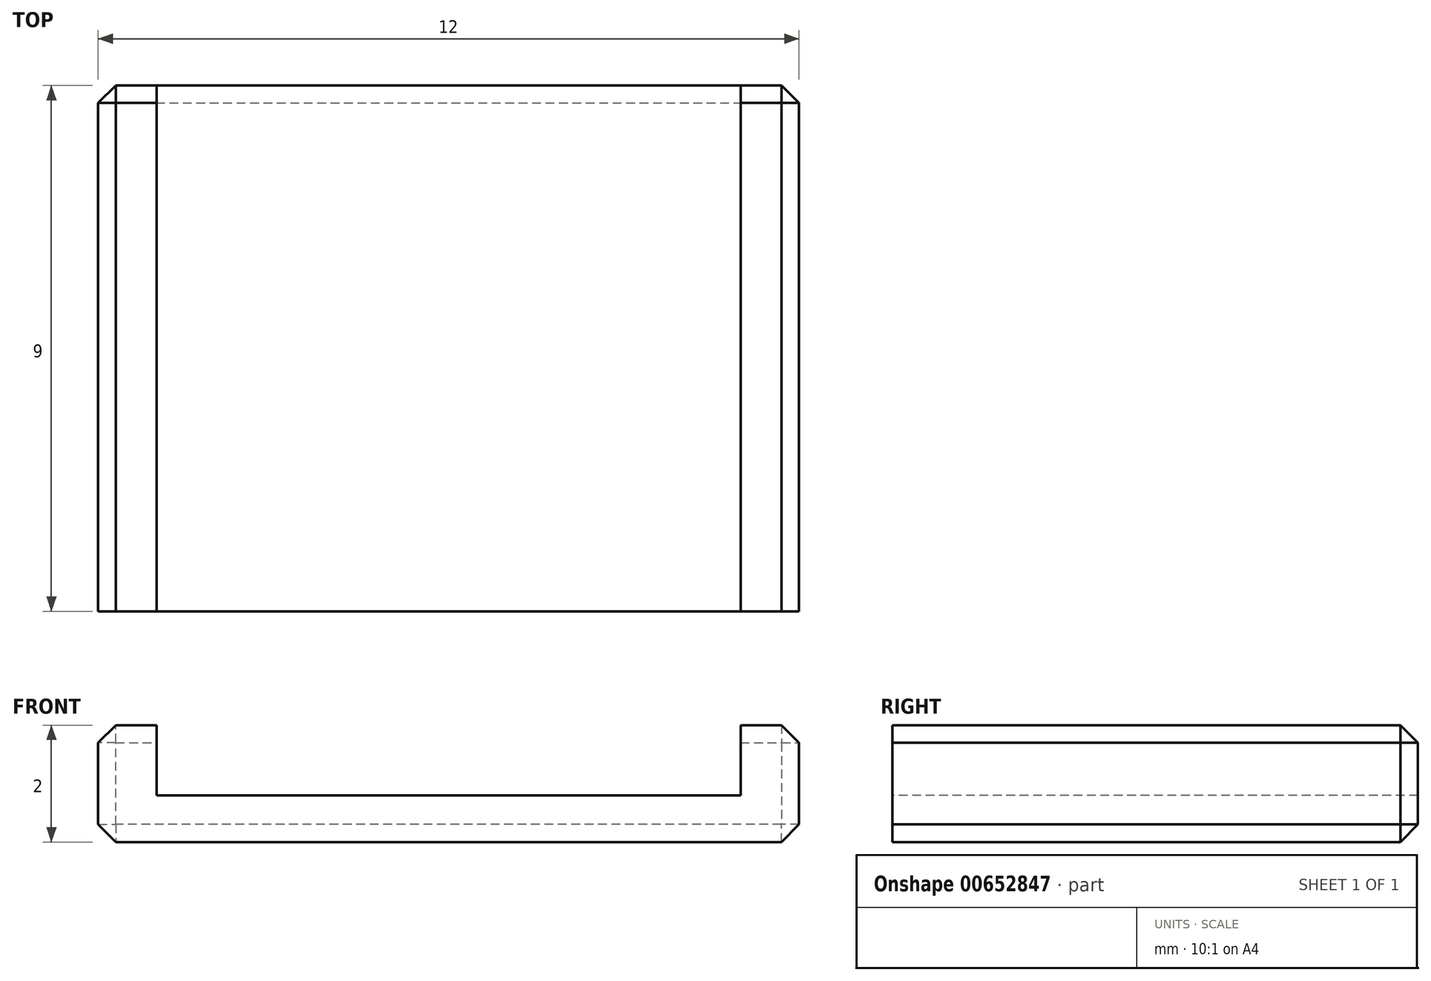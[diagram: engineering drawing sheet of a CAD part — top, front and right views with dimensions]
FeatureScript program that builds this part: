
annotation { "Feature Type Name" : "Feature", "Feature Type Description" : "" }
export const myFeature = defineFeature(function(context is Context, id is Id, definition is map)
    precondition{}
    {
        {
            var Q0;
            Q0=qCreatedBy(makeId("Top.planeOp"),FACE);
            var sketch = newSketch(context, id + "F0", { "sketchPlane" : qUnion([Q0])});
            skLineSegment(sketch, "E0.bottom", {"start": v(-6, 0) * mm, "end": v(6, 0) * mm});
            skLineSegment(sketch, "E0.top", {"start": v(-6, -9) * mm, "end": v(6, -9) * mm});
            skLineSegment(sketch, "E0.left", {"start": v(-6, 0) * mm, "end": v(-6, -9) * mm});
            skLineSegment(sketch, "E0.right", {"start": v(6, 0) * mm, "end": v(6, -9) * mm});
            skSolve(sketch);
        }
        {
            var Q0;
            Q0 = qSketchRegion(id + "F0", true);
            extrude(context, id + "F1", {"entities" : qUnion([Q0]), "depth" : 2 * mm, "offsetDistance" : 25 * mm});
        }
        {
            var Q0;
            Q0=makeQuery(id+"F1.opExtrude","CAP_FACE",FACE,{"disambiguationData":[OSD([sQuery(id+"F0.wireOp",EDGE,"E0.bottom"),sQuery(id+"F0.wireOp",EDGE,"E0.top"),sQuery(id+"F0.wireOp",EDGE,"E0.left"),sQuery(id+"F0.wireOp",EDGE,"E0.right")])],"isStart":false});
            var sketch = newSketch(context, id + "F2", { "sketchPlane" : qUnion([Q0])});
            skLineSegment(sketch, "E1.bottom", {"start": v(-5, 0) * mm, "end": v(5, 0) * mm});
            skLineSegment(sketch, "E1.top", {"start": v(-5, -9) * mm, "end": v(5, -9) * mm});
            skLineSegment(sketch, "E1.left", {"start": v(-5, 0) * mm, "end": v(-5, -9) * mm});
            skLineSegment(sketch, "E1.right", {"start": v(5, 0) * mm, "end": v(5, -9) * mm});
            skSolve(sketch);
        }
        {
            var Q0;
            Q0=makeQuery(id+"F2.imprint","IMPRINT",FACE,{"disambiguationData":[TD([[makeQuery(id+"F2.imprint","IMPRINT",EDGE,{"derivedFrom":sQuery(id+"F2.wireOp",EDGE,"E1.bottom")}),-1.0]])]});
            extrude(context, id + "F3", {"entities" : qUnion([Q0]), "operationType" : NewBodyOperationType.REMOVE, "oppositeDirection" : true, "depth" : 1.2 * mm, "offsetDistance" : 25 * mm});
        }
        {
            var Q0;
            Q0=makeQuery(id+"F1.opExtrude","CAP_EDGE",EDGE,{"disambiguationData":[OSD([sQuery(id+"F0.wireOp",EDGE,"E0.left")])],"isStart":false});
            var Q1;
            Q1=makeQuery(id+"F1.opExtrude","CAP_EDGE",EDGE,{"disambiguationData":[OSD([sQuery(id+"F0.wireOp",EDGE,"E0.right")])],"isStart":false});
            var Q2;
            Q2=makeQuery(id+"F1.opExtrude","CAP_EDGE",EDGE,{"disambiguationData":[OSD([sQuery(id+"F0.wireOp",EDGE,"E0.right")])],"isStart":true});
            var Q3;
            Q3=makeQuery(id+"F1.opExtrude","CAP_EDGE",EDGE,{"disambiguationData":[OSD([sQuery(id+"F0.wireOp",EDGE,"E0.left")])],"isStart":true});
            var Q4;
            Q4=makeQuery(id+"F1.opExtrude","CAP_EDGE",EDGE,{"disambiguationData":[OSD([sQuery(id+"F0.wireOp",EDGE,"E0.bottom")])],"isStart":true});
            var Q5;
            Q5=makeQuery(id+"F1.opExtrude","SWEPT_EDGE",EDGE,{"disambiguationData":[OSD([sQuery(id+"F0.wireOp",EDGE,"E0.bottom"),sQuery(id+"F0.wireOp",EDGE,"E0.left")])]});
            var Q6;
            {var subQ0=sQuery(id+"F0.wireOp",EDGE,"E0.bottom");var subQ1=sQuery(id+"F0.wireOp",EDGE,"E0.left");Q6=makeQuery(id+"F3.boolean.opBoolean","SPLIT",EDGE,{"disambiguationData":[TD([makeQuery(id+"F1.opExtrude","SWEPT_FACE",FACE,{"disambiguationData":[OSD([subQ1])]})])],"derivedFrom":makeQuery(id+"F1.opExtrude","CAP_EDGE",EDGE,{"disambiguationData":[OSD([subQ0])],"isStart":false})});}
            var Q7;
            Q7=makeQuery(id+"F1.opExtrude","SWEPT_EDGE",EDGE,{"disambiguationData":[OSD([sQuery(id+"F0.wireOp",EDGE,"E0.bottom"),sQuery(id+"F0.wireOp",EDGE,"E0.right")])]});
            var Q8;
            {var subQ0=sQuery(id+"F0.wireOp",EDGE,"E0.bottom");var subQ1=sQuery(id+"F0.wireOp",EDGE,"E0.right");Q8=makeQuery(id+"F3.boolean.opBoolean","SPLIT",EDGE,{"disambiguationData":[TD([makeQuery(id+"F1.opExtrude","SWEPT_FACE",FACE,{"disambiguationData":[OSD([subQ1])]})])],"derivedFrom":makeQuery(id+"F1.opExtrude","CAP_EDGE",EDGE,{"disambiguationData":[OSD([subQ0])],"isStart":false})});}
            chamfer(context, id + "F4", {"entities" : qUnion([Q0, Q1, Q2, Q3, Q4, Q5, Q6, Q7, Q8]), "width" : .3 * mm, "tangentPropagation" : true});
        }
    });
